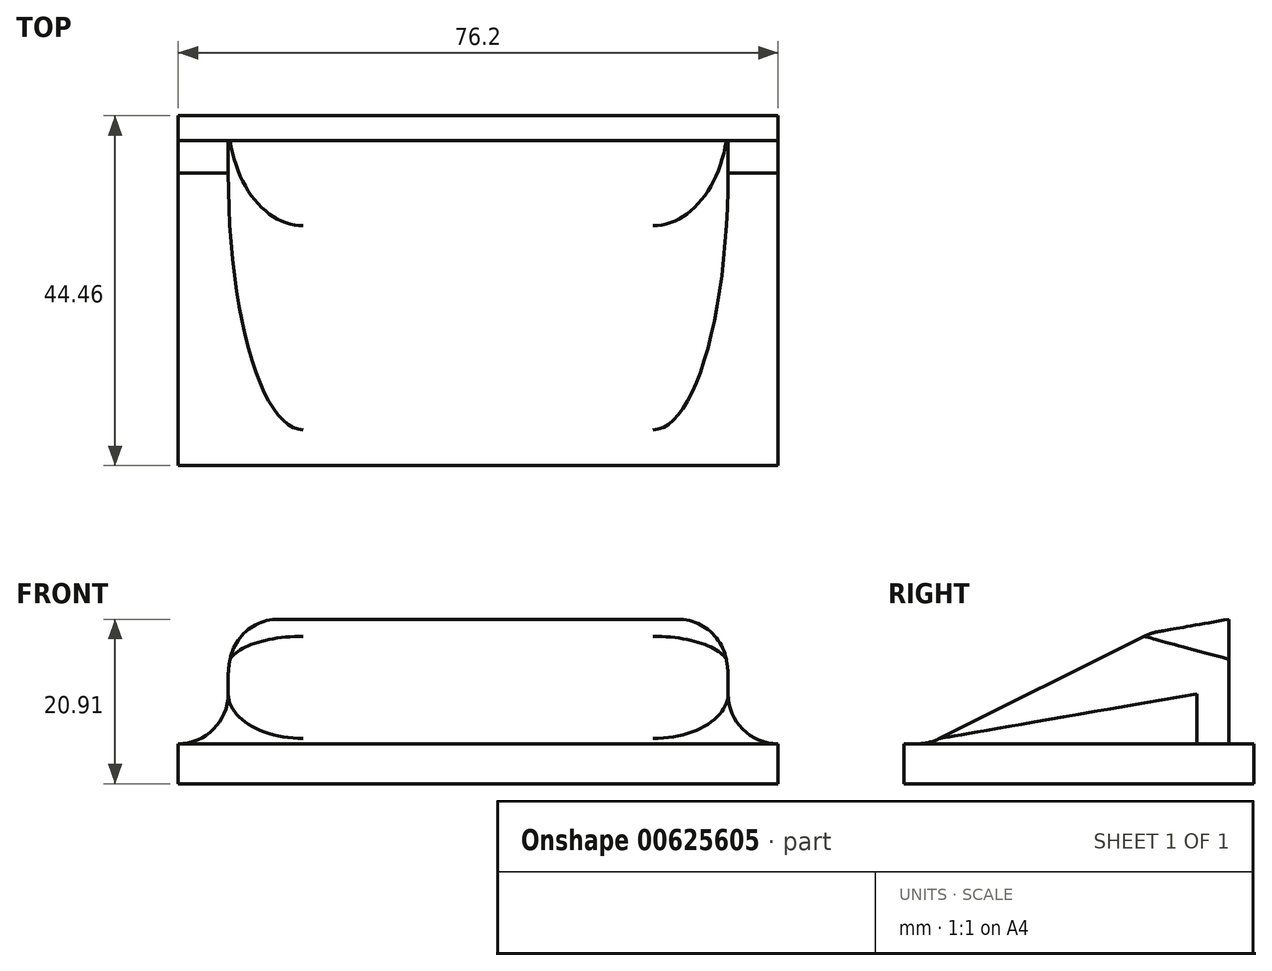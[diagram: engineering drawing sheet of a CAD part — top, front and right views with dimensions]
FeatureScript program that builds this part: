
annotation { "Feature Type Name" : "Feature", "Feature Type Description" : "" }
export const myFeature = defineFeature(function(context is Context, id is Id, definition is map)
    precondition{}
    {
        {
            var Q0;
            Q0=qCreatedBy(makeId("Top.planeOp"),FACE);
            var sketch = newSketch(context, id + "F0", { "sketchPlane" : qUnion([Q0])});
            skLineSegment(sketch, "E0.bottom", {"start": v(-38.1, 22.22) * mm, "end": v(38.1, 22.23) * mm});
            skLineSegment(sketch, "E0.top", {"start": v(-38.1, -22.23) * mm, "end": v(38.1, -22.23) * mm});
            skLineSegment(sketch, "E0.left", {"start": v(-38.1, 22.23) * mm, "end": v(-38.1, -22.23) * mm});
            skLineSegment(sketch, "E0.right", {"start": v(38.1, 22.23) * mm, "end": v(38.1, -22.23) * mm});
            skLineSegment(sketch, "E1", {"start": v(-38.1, 0) * mm, "end": v(38.1, 0) * mm, "construction": true});
            skLineSegment(sketch, "E2", {"start": v(0, 22.23) * mm, "end": v(0, -22.23) * mm, "construction": true});
            skSolve(sketch);
        }
        {
            var Q0;
            Q0=qSketchRegion(id+"F0",true);
            extrude(context, id + "F1", {"entities" : qUnion([Q0]), "depth" : 5.08 * mm});
        }
        {
            var Q0;
            Q0=qCreatedBy(makeId("Right.planeOp"),FACE);
            var sketch = newSketch(context, id + "F2", { "sketchPlane" : qUnion([Q0])});
            skLineSegment(sketch, "E3", {"start": v(-19.05, 5.08) * mm, "end": v(19.05, 24.13) * mm});
            skLineSegment(sketch, "E4", {"start": v(19.05, 5.08) * mm, "end": v(19.05, 24.13) * mm});
            skLineSegment(sketch, "E5", {"start": v(19.05, 5.08) * mm, "end": v(-19.05, 5.08) * mm});
            skLineSegment(sketch, "E6", {"start": v(0, 14.6) * mm, "end": v(0, 5.08) * mm, "construction": true});
            skSolve(sketch);
        }
        {
            var Q0;
            Q0=qSketchRegion(id+"F2",true);
            extrude(context, id + "F3", {"entities" : qUnion([Q0]), "operationType" : NewBodyOperationType.ADD, "depth" : 31.75 * mm, "hasSecondDirection" : true, "secondDirectionOppositeDirection" : true, "secondDirectionDepth" : 31.75 * mm});
        }
        {
            var Q0;
            Q0=makeQuery(id+"F3.opExtrude","CAP_EDGE",EDGE,{"disambiguationData":[OSD([sQuery(id+"F2.wireOp",EDGE,"E3")])],"isStart":false});
            var Q1;
            Q1=makeQuery(id+"F3.opExtrude","CAP_EDGE",EDGE,{"disambiguationData":[OSD([sQuery(id+"F2.wireOp",EDGE,"E3")])],"isStart":true});
            fillet(context, id + "F4", {"entities" : qUnion([Q0, Q1]), "radius" : 9.52 * mm, "tangentPropagation" : true, "allowEdgeOverflow" : false});
        }
        {
            var Q0;
            Q0=makeQuery(id+"F3.opExtrude","CAP_FACE",FACE,{"disambiguationData":[OSD([sQuery(id+"F2.wireOp",EDGE,"E3"),sQuery(id+"F2.wireOp",EDGE,"E4"),sQuery(id+"F2.wireOp",EDGE,"E5")])],"isStart":false});
            var sketch = newSketch(context, id + "F5", { "sketchPlane" : qUnion([Q0])});
            skLineSegment(sketch, "E7.top", {"start": v(50.3, 45.12) * mm, "end": v(-23.54, 45.12) * mm});
            skLineSegment(sketch, "E7.right", {"start": v(-23.54, 13.4) * mm, "end": v(-23.54, 45.12) * mm});
            skLineSegment(sketch, "E8", {"start": v(-23.54, 13.4) * mm, "end": v(52.06, 26.73) * mm});
            skLineSegment(sketch, "E9", {"start": v(52.06, 26.73) * mm, "end": v(50.3, 45.12) * mm});
            skSolve(sketch);
        }
        {
            var Q0;
            Q0=qSketchRegion(id+"F5",true);
            extrude(context, id + "F6", {"entities" : qUnion([Q0]), "operationType" : NewBodyOperationType.REMOVE, "endBound" : BoundingType.THROUGH_ALL, "oppositeDirection" : true, "depth" : 25.4 * mm});
        }
        {
            var Q0;
            {var subQ0=sQuery(id+"F2.wireOp",EDGE,"E3");Q0=makeQuery(id+"F6.boolean.opBoolean","INTERSECT",EDGE,{"derivedFrom":[makeQuery(id+"F4.opFillet","BLEND_FACE",FACE,{"disambiguationData":[OSD([subQ0]),TDD([makeQuery(id+"F3.opExtrude","CAP_EDGE",EDGE,{"disambiguationData":[OSD([subQ0])],"isStart":false})])]}),makeQuery(id+"F6.opExtrude","SWEPT_FACE",FACE,{"disambiguationData":[OSD([sQuery(id+"F5.wireOp",EDGE,"E8")])]})]});}
            var Q1;
            {var subQ0=sQuery(id+"F2.wireOp",EDGE,"E3");Q1=makeQuery(id+"F6.boolean.opBoolean","INTERSECT",EDGE,{"derivedFrom":[makeQuery(id+"F4.opFillet","BLEND_FACE",FACE,{"disambiguationData":[OSD([subQ0]),TDD([makeQuery(id+"F3.opExtrude","CAP_EDGE",EDGE,{"disambiguationData":[OSD([subQ0])],"isStart":true})])]}),makeQuery(id+"F6.opExtrude","SWEPT_FACE",FACE,{"disambiguationData":[OSD([sQuery(id+"F5.wireOp",EDGE,"E8")])]})]});}
            var Q2;
            Q2=makeQuery(id+"F6.boolean.opBoolean","INTERSECT",EDGE,{"derivedFrom":[makeQuery(id+"F3.opExtrude","SWEPT_FACE",FACE,{"disambiguationData":[OSD([sQuery(id+"F2.wireOp",EDGE,"E3")])]}),makeQuery(id+"F6.opExtrude","SWEPT_FACE",FACE,{"disambiguationData":[OSD([sQuery(id+"F5.wireOp",EDGE,"E8")])]})]});
            fillet(context, id + "F7", {"entities" : qUnion([Q0, Q1, Q2]), "radius" : 6.35 * mm, "allowEdgeOverflow" : false});
        }
        {
            var Q0;
            Q0=makeQuery(id+"F3.opExtrude","CAP_EDGE",EDGE,{"disambiguationData":[OSD([sQuery(id+"F2.wireOp",EDGE,"E5")])],"isStart":false});
            var Q1;
            Q1=makeQuery(id+"F4.opFillet","BLEND_EDGE",EDGE,{"blendedFrom":[makeQuery(id+"F3.opExtrude","CAP_EDGE",EDGE,{"disambiguationData":[OSD([sQuery(id+"F2.wireOp",EDGE,"E3")])],"isStart":false}),makeQuery(id+"F1.opExtrude","CAP_FACE",FACE,{"disambiguationData":[OSD([sQuery(id+"F0.wireOp",EDGE,"E0.bottom"),sQuery(id+"F0.wireOp",EDGE,"E0.top"),sQuery(id+"F0.wireOp",EDGE,"E0.left"),sQuery(id+"F0.wireOp",EDGE,"E0.right")])],"isStart":false})],"blendedInto":[makeQuery(id+"F1.opExtrude","CAP_FACE",FACE,{"disambiguationData":[OSD([sQuery(id+"F0.wireOp",EDGE,"E0.bottom"),sQuery(id+"F0.wireOp",EDGE,"E0.top"),sQuery(id+"F0.wireOp",EDGE,"E0.left"),sQuery(id+"F0.wireOp",EDGE,"E0.right")])],"isStart":false})]});
            fillet(context, id + "F8", {"entities" : qUnion([Q0, Q1]), "radius" : 6.35 * mm, "tangentPropagation" : true, "allowEdgeOverflow" : false});
        }
    });
